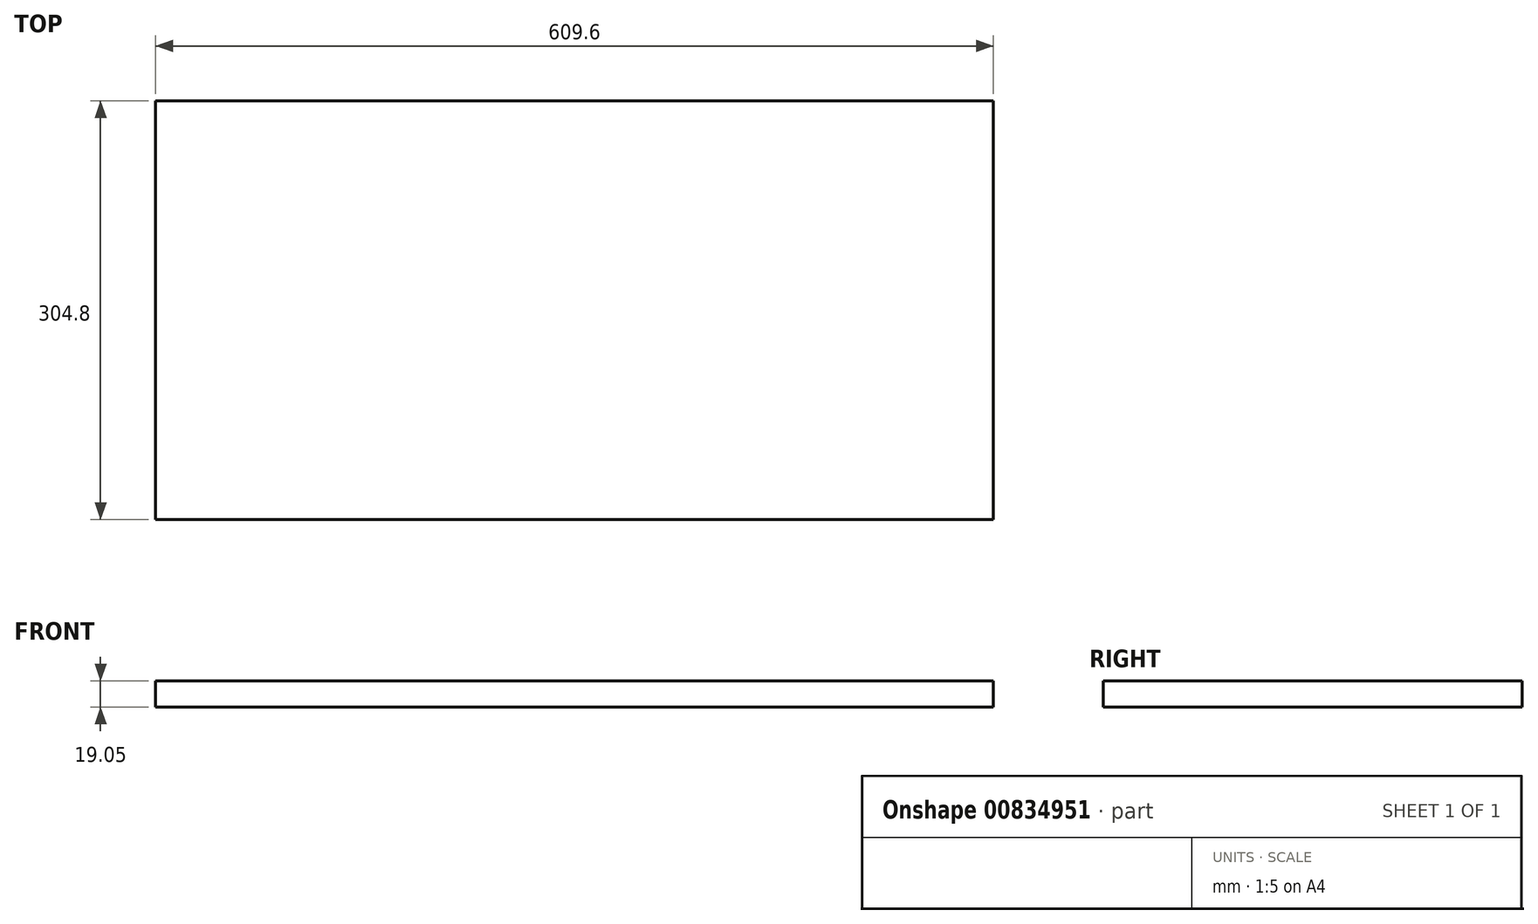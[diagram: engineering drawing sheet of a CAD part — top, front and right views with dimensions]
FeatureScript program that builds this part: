
annotation { "Feature Type Name" : "Feature", "Feature Type Description" : "" }
export const myFeature = defineFeature(function(context is Context, id is Id, definition is map)
    precondition{}
    {
        {
            var Q0;
            Q0=qCreatedBy(makeId("Top.planeOp"),FACE);
            var sketch = newSketch(context, id + "F0", { "sketchPlane" : qUnion([Q0])});
            skLineSegment(sketch, "E0.bottom", {"start": v(0, 0) * mm, "end": v(609.6, 0) * mm});
            skLineSegment(sketch, "E0.top", {"start": v(0, 304.8) * mm, "end": v(609.6, 304.8) * mm});
            skLineSegment(sketch, "E0.left", {"start": v(0, 0) * mm, "end": v(0, 304.8) * mm});
            skLineSegment(sketch, "E0.right", {"start": v(609.6, 0) * mm, "end": v(609.6, 304.8) * mm});
            skSolve(sketch);
        }
        {
            var Q0;
            Q0=makeQuery(id+"F0.imprint","IMPRINT",FACE,{"disambiguationData":[TD([[makeQuery(id+"F0.imprint","IMPRINT",EDGE,{"derivedFrom":sQuery(id+"F0.wireOp",EDGE,"E0.bottom")}),1.0]])]});
            extrude(context, id + "F1", {"entities" : qUnion([Q0]), "depth" : 19.05 * mm, "offsetDistance" : 25.4 * mm});
        }
    });
